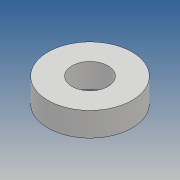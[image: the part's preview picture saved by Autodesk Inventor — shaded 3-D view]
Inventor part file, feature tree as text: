
AUTODESK INVENTOR PART (.ipt)
format: ipt  version: 2017 (Build 210142000, 142)  size: 79,872 bytes
history: native  units: mm
features: other x1, extrude x1, sketch x1
ambient origin geometry x8: Origin, YZ Plane, XZ Plane, XY Plane, X Axis, Y Axis, Z Axis, Center Point
bodies: Body1 (feature_tree)
feature tree (3):
  other  "Sólido1"
  extrude  "Extrusión1"  Depth=6.0mm
  sketch  "Boceto1"  dims[d0=6.0mm d1=9.0mm d2=6.0mm d3=0.0mm]
